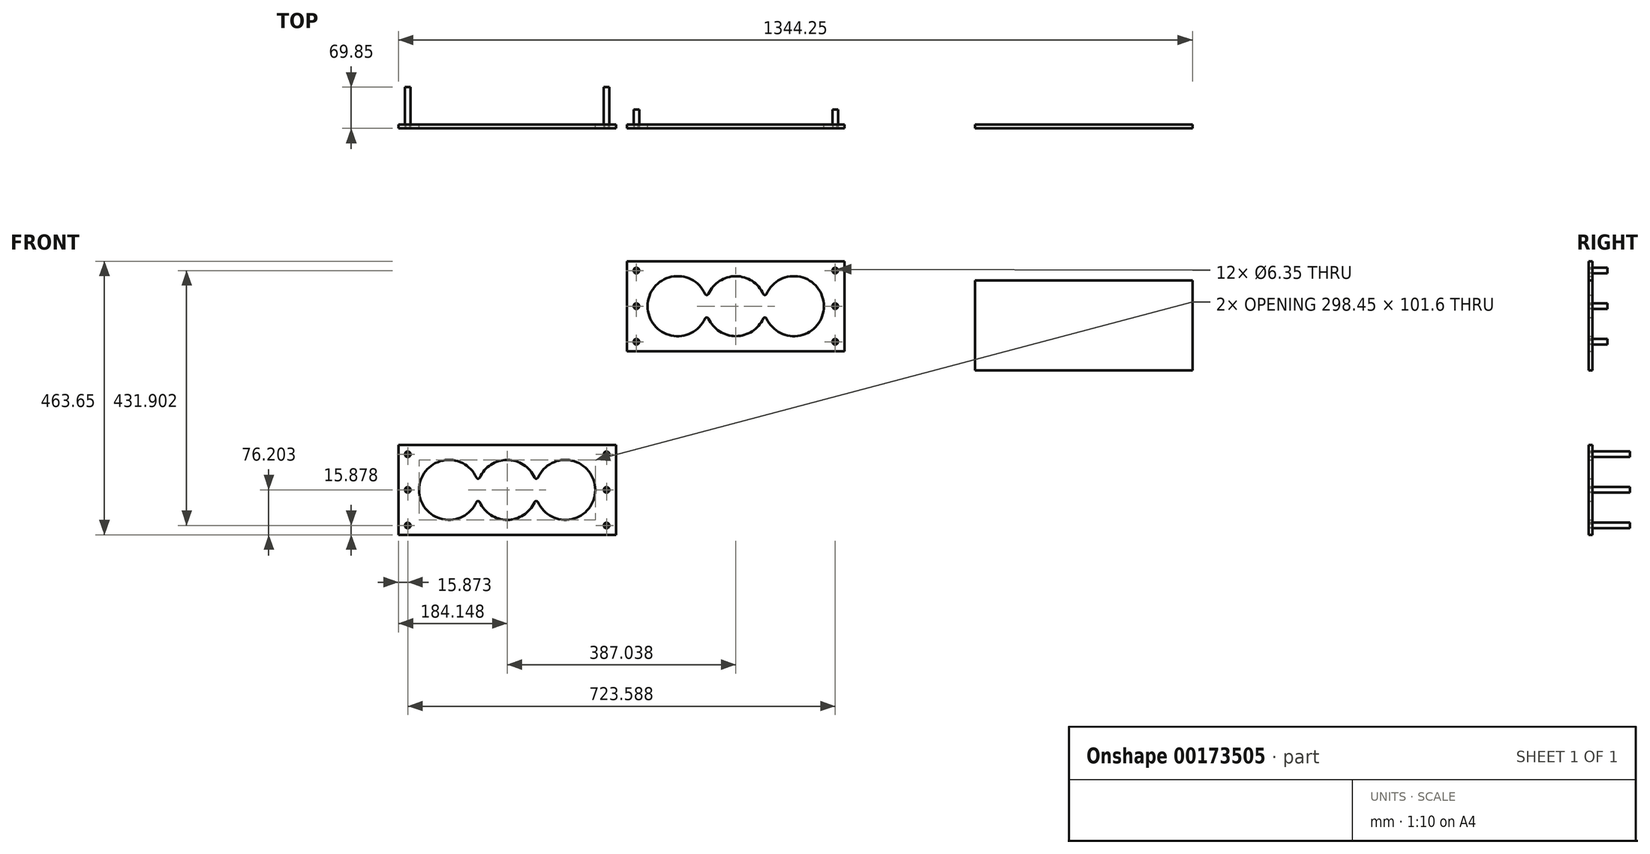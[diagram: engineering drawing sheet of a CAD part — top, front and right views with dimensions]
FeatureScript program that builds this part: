
annotation { "Feature Type Name" : "Feature", "Feature Type Description" : "" }
export const myFeature = defineFeature(function(context is Context, id is Id, definition is map)
    precondition{}
    {
        {
            var Q0;
            Q0=qCreatedBy(makeId("Front.planeOp"),FACE);
            var sketch = newSketch(context, id + "F0", { "sketchPlane" : qUnion([Q0])});
            skLineSegment(sketch, "E0.bottom", {"start": v(-251.83, 93.22) * mm, "end": v(116.47, 93.22) * mm});
            skLineSegment(sketch, "E0.top", {"start": v(-251.83, -59.18) * mm, "end": v(116.47, -59.18) * mm});
            skLineSegment(sketch, "E0.left", {"start": v(-251.83, 93.22) * mm, "end": v(-251.83, -59.18) * mm});
            skLineSegment(sketch, "E0.right", {"start": v(116.47, 93.22) * mm, "end": v(116.47, -59.18) * mm});
            skLineSegment(sketch, "E1.left", {"start": v(-251.83, 17.02) * mm, "end": v(-251.83, 17.02) * mm});
            skLineSegment(sketch, "E1.right", {"start": v(116.47, 17.02) * mm, "end": v(116.47, 17.02) * mm});
            skArc(sketch, "E2", {"start": v(-114, -3.84) * mm, "mid": v(-67.68, -33.78) * mm, "end": v(-21.37, -3.84) * mm});
            skLineSegment(sketch, "E3", {"start": v(-67.68, 17.02) * mm, "end": v(30.74, 17.02) * mm, "construction": true});
            skArc(sketch, "E4", {"start": v(-15.58, -3.84) * mm, "mid": v(81.54, 17.02) * mm, "end": v(-15.58, 37.89) * mm});
            skArc(sketch, "E5.MirrorC", {"start": v(-119.8, -3.84) * mm, "mid": v(-216.9, 17.02) * mm, "end": v(-119.8, 37.89) * mm});
            skCircle(sketch, "E6", {"center": v(-166.1, 17.02) * mm, "radius": 43.66 * mm, "construction": true});
            skCircle(sketch, "E7", {"center": v(-67.68, 17.02) * mm, "radius": 43.66 * mm, "construction": true});
            skCircle(sketch, "E8", {"center": v(30.74, 17.02) * mm, "radius": 43.66 * mm, "construction": true});
            skPoint(sketch, "E9.visualSharp", {"position": v(-116.9, 29.63) * mm});
            skArc(sketch, "E9.filletArc", {"start": v(-119.8, 37.89) * mm, "mid": v(-116.9, 36.02) * mm, "end": v(-114, 37.89) * mm});
            skPoint(sketch, "E10.visualSharp", {"position": v(-116.9, 4.42) * mm});
            skArc(sketch, "E10.filletArc", {"start": v(-114, -3.84) * mm, "mid": v(-116.9, -1.97) * mm, "end": v(-119.8, -3.84) * mm});
            skArc(sketch, "E11.trimOffspring", {"start": v(-21.37, 37.89) * mm, "mid": v(-67.68, 67.82) * mm, "end": v(-114, 37.89) * mm});
            skPoint(sketch, "E12.visualSharp", {"position": v(-18.47, 29.63) * mm});
            skArc(sketch, "E12.filletArc", {"start": v(-21.37, 37.89) * mm, "mid": v(-18.47, 36.02) * mm, "end": v(-15.58, 37.89) * mm});
            skPoint(sketch, "E13.visualSharp", {"position": v(-18.47, 4.42) * mm});
            skArc(sketch, "E13.filletArc", {"start": v(-15.58, -3.84) * mm, "mid": v(-18.47, -1.97) * mm, "end": v(-21.37, -3.84) * mm});
            skCircle(sketch, "E14", {"center": v(-235.96, 77.35) * mm, "radius": 3.18 * mm});
            skCircle(sketch, "E15", {"center": v(-235.96, -43.3) * mm, "radius": 3.18 * mm});
            skCircle(sketch, "E16", {"center": v(100.6, 77.35) * mm, "radius": 3.18 * mm});
            skCircle(sketch, "E17", {"center": v(100.6, -43.3) * mm, "radius": 3.18 * mm});
            skCircle(sketch, "E18", {"center": v(100.6, 17.02) * mm, "radius": 3.18 * mm});
            skCircle(sketch, "E19", {"center": v(-235.96, 17.02) * mm, "radius": 3.18 * mm});
            skSolve(sketch);
        }
        {
            var Q0;
            Q0 = qSketchRegion(id + "F0", true);
            extrude(context, id + "F1", {"entities" : qUnion([Q0]), "depth" : 6.35 * mm});
        }
        {
            var Q0;
            Q0=makeQuery(id+"F1.opExtrude","CAP_FACE",FACE,{"disambiguationData":[OSD([sQuery(id+"F0.wireOp",EDGE,"E0.bottom"),sQuery(id+"F0.wireOp",EDGE,"E0.top"),sQuery(id+"F0.wireOp",EDGE,"E0.left"),sQuery(id+"F0.wireOp",EDGE,"E0.right"),sQuery(id+"F0.wireOp",EDGE,"E2"),sQuery(id+"F0.wireOp",EDGE,"E4"),sQuery(id+"F0.wireOp",EDGE,"E5.MirrorC"),sQuery(id+"F0.wireOp",EDGE,"E9.filletArc"),sQuery(id+"F0.wireOp",EDGE,"E10.filletArc"),sQuery(id+"F0.wireOp",EDGE,"E11.trimOffspring"),sQuery(id+"F0.wireOp",EDGE,"E12.filletArc"),sQuery(id+"F0.wireOp",EDGE,"E13.filletArc"),sQuery(id+"F0.wireOp",EDGE,"E14"),sQuery(id+"F0.wireOp",EDGE,"E15"),sQuery(id+"F0.wireOp",EDGE,"E16"),sQuery(id+"F0.wireOp",EDGE,"E17"),sQuery(id+"F0.wireOp",EDGE,"E18"),sQuery(id+"F0.wireOp",EDGE,"E19")])],"isStart":false});
            var sketch = newSketch(context, id + "F2", { "sketchPlane" : qUnion([Q0])});
            skCircle(sketch, "E20", {"center": v(-235.96, 77.35) * mm, "radius": 4.76 * mm});
            skCircle(sketch, "E21", {"center": v(-235.96, 17.02) * mm, "radius": 4.76 * mm});
            skCircle(sketch, "E22", {"center": v(-235.96, -43.3) * mm, "radius": 4.76 * mm});
            skCircle(sketch, "E23", {"center": v(100.6, 77.35) * mm, "radius": 4.76 * mm});
            skCircle(sketch, "E24", {"center": v(100.6, 17.02) * mm, "radius": 4.76 * mm});
            skCircle(sketch, "E25", {"center": v(100.6, -43.3) * mm, "radius": 4.76 * mm});
            skSolve(sketch);
        }
        {
            var Q0;
            Q0 = qSketchRegion(id + "F2", true);
            extrude(context, id + "F3", {"entities" : qUnion([Q0]), "depth" : -31.75 * mm});
        }
        {
            var Q0;
            Q0=qCreatedBy(makeId("Front.planeOp"),FACE);
            var sketch = newSketch(context, id + "F4", { "sketchPlane" : qUnion([Q0])});
            skLineSegment(sketch, "E26.bottom", {"start": v(337.08, 60.51) * mm, "end": v(705.38, 60.51) * mm});
            skLineSegment(sketch, "E26.top", {"start": v(337.08, -91.89) * mm, "end": v(705.38, -91.89) * mm});
            skLineSegment(sketch, "E26.left", {"start": v(337.08, 60.51) * mm, "end": v(337.08, -91.89) * mm});
            skLineSegment(sketch, "E26.right", {"start": v(705.38, 60.51) * mm, "end": v(705.38, -91.89) * mm});
            skSolve(sketch);
        }
        {
            var Q0;
            Q0 = qSketchRegion(id + "F4", true);
            extrude(context, id + "F5", {"entities" : qUnion([Q0]), "depth" : 6.35 * mm});
        }
        {
            var Q0;
            Q0=qCreatedBy(makeId("Front.planeOp"),FACE);
            var sketch = newSketch(context, id + "F6", { "sketchPlane" : qUnion([Q0])});
            skLineSegment(sketch, "E27.bottom", {"start": v(-638.87, -218.03) * mm, "end": v(-270.57, -218.03) * mm});
            skLineSegment(sketch, "E27.top", {"start": v(-638.87, -370.43) * mm, "end": v(-270.57, -370.43) * mm});
            skLineSegment(sketch, "E27.left", {"start": v(-638.87, -218.03) * mm, "end": v(-638.87, -370.43) * mm});
            skLineSegment(sketch, "E27.right", {"start": v(-270.57, -218.03) * mm, "end": v(-270.57, -370.43) * mm});
            skLineSegment(sketch, "E28.left", {"start": v(-638.87, -294.23) * mm, "end": v(-638.87, -294.23) * mm});
            skLineSegment(sketch, "E28.right", {"start": v(-270.57, -294.23) * mm, "end": v(-270.57, -294.23) * mm});
            skArc(sketch, "E29", {"start": v(-501.04, -315.1) * mm, "mid": v(-454.72, -345.03) * mm, "end": v(-408.4, -315.1) * mm});
            skLineSegment(sketch, "E30", {"start": v(-454.72, -294.23) * mm, "end": v(-356.3, -294.23) * mm, "construction": true});
            skArc(sketch, "E31", {"start": v(-402.61, -315.1) * mm, "mid": v(-305.5, -294.23) * mm, "end": v(-402.61, -273.36) * mm});
            skArc(sketch, "E32.MirrorC", {"start": v(-506.83, -315.1) * mm, "mid": v(-603.95, -294.23) * mm, "end": v(-506.83, -273.36) * mm});
            skCircle(sketch, "E33", {"center": v(-553.15, -294.23) * mm, "radius": 43.66 * mm, "construction": true});
            skCircle(sketch, "E34", {"center": v(-454.72, -294.23) * mm, "radius": 43.66 * mm, "construction": true});
            skCircle(sketch, "E35", {"center": v(-356.3, -294.23) * mm, "radius": 43.66 * mm, "construction": true});
            skPoint(sketch, "E36.visualSharp", {"position": v(-503.93, -281.63) * mm});
            skArc(sketch, "E36.filletArc", {"start": v(-506.83, -273.36) * mm, "mid": v(-503.93, -275.23) * mm, "end": v(-501.04, -273.36) * mm});
            skPoint(sketch, "E37.visualSharp", {"position": v(-503.93, -306.83) * mm});
            skArc(sketch, "E37.filletArc", {"start": v(-501.04, -315.1) * mm, "mid": v(-503.93, -313.22) * mm, "end": v(-506.83, -315.1) * mm});
            skArc(sketch, "E38.trimOffspring", {"start": v(-408.4, -273.36) * mm, "mid": v(-454.72, -243.43) * mm, "end": v(-501.04, -273.36) * mm});
            skPoint(sketch, "E39.visualSharp", {"position": v(-405.5, -281.63) * mm});
            skArc(sketch, "E39.filletArc", {"start": v(-408.4, -273.36) * mm, "mid": v(-405.5, -275.23) * mm, "end": v(-402.61, -273.36) * mm});
            skPoint(sketch, "E40.visualSharp", {"position": v(-405.5, -306.83) * mm});
            skArc(sketch, "E40.filletArc", {"start": v(-402.61, -315.1) * mm, "mid": v(-405.5, -313.22) * mm, "end": v(-408.4, -315.1) * mm});
            skCircle(sketch, "E41", {"center": v(-623, -233.9) * mm, "radius": 3.18 * mm});
            skCircle(sketch, "E42", {"center": v(-623, -354.55) * mm, "radius": 3.18 * mm});
            skCircle(sketch, "E43", {"center": v(-286.45, -233.9) * mm, "radius": 3.18 * mm});
            skCircle(sketch, "E44", {"center": v(-286.45, -354.55) * mm, "radius": 3.18 * mm});
            skCircle(sketch, "E45", {"center": v(-286.45, -294.23) * mm, "radius": 3.18 * mm});
            skCircle(sketch, "E46", {"center": v(-623, -294.23) * mm, "radius": 3.18 * mm});
            skSolve(sketch);
        }
        {
            var Q0;
            Q0 = qSketchRegion(id + "F6", true);
            extrude(context, id + "F7", {"entities" : qUnion([Q0]), "depth" : 6.35 * mm});
        }
        {
            var Q0;
            Q0=makeQuery(id+"F7.opExtrude","CAP_FACE",FACE,{"disambiguationData":[OSD([sQuery(id+"F6.wireOp",EDGE,"E27.bottom"),sQuery(id+"F6.wireOp",EDGE,"E27.top"),sQuery(id+"F6.wireOp",EDGE,"E27.left"),sQuery(id+"F6.wireOp",EDGE,"E27.right"),sQuery(id+"F6.wireOp",EDGE,"E29"),sQuery(id+"F6.wireOp",EDGE,"E31"),sQuery(id+"F6.wireOp",EDGE,"E32.MirrorC"),sQuery(id+"F6.wireOp",EDGE,"E36.filletArc"),sQuery(id+"F6.wireOp",EDGE,"E37.filletArc"),sQuery(id+"F6.wireOp",EDGE,"E38.trimOffspring"),sQuery(id+"F6.wireOp",EDGE,"E39.filletArc"),sQuery(id+"F6.wireOp",EDGE,"E40.filletArc"),sQuery(id+"F6.wireOp",EDGE,"E41"),sQuery(id+"F6.wireOp",EDGE,"E42"),sQuery(id+"F6.wireOp",EDGE,"E43"),sQuery(id+"F6.wireOp",EDGE,"E44"),sQuery(id+"F6.wireOp",EDGE,"E45"),sQuery(id+"F6.wireOp",EDGE,"E46")])],"isStart":false});
            var sketch = newSketch(context, id + "F8", { "sketchPlane" : qUnion([Q0])});
            skCircle(sketch, "E47", {"center": v(-623, -233.9) * mm, "radius": 4.76 * mm});
            skCircle(sketch, "E48", {"center": v(-623, -294.23) * mm, "radius": 4.76 * mm});
            skCircle(sketch, "E49", {"center": v(-623, -354.55) * mm, "radius": 4.76 * mm});
            skCircle(sketch, "E50", {"center": v(-286.45, -233.9) * mm, "radius": 4.76 * mm});
            skCircle(sketch, "E51", {"center": v(-286.45, -294.23) * mm, "radius": 4.76 * mm});
            skCircle(sketch, "E52", {"center": v(-286.45, -354.55) * mm, "radius": 4.76 * mm});
            skSolve(sketch);
        }
        {
            var Q0;
            Q0 = qSketchRegion(id + "F8", true);
            extrude(context, id + "F9", {"entities" : qUnion([Q0]), "depth" : -69.85 * mm});
        }
    });
